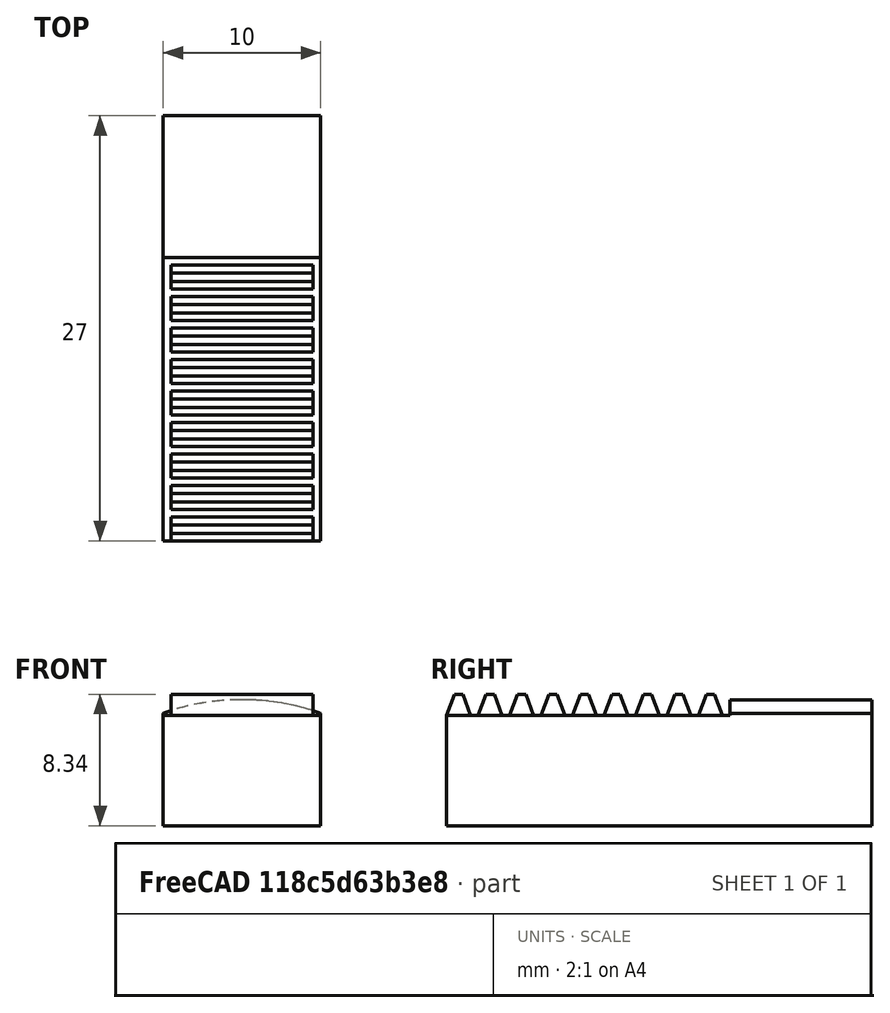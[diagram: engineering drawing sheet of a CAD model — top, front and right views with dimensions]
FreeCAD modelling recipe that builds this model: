
FCSTD DOCUMENT  (FreeCAD 0.16R4924 (Git))
Label: pin_v3p2
License: All rights reserved
LicenseURL: http://en.wikipedia.org/wiki/All_rights_reserved
objects: Part::Feature×9, Part::Box×3, Part::MultiFuse×2, Part::Cylinder×1, Part::MultiCommon×1, Part::Cut×1
note: 17 computed .brp shape members not serialized (recipe doc carries the construction recipe); baked Part::Feature solids carry a one-line shape summary decoded from their .brp

FEATURE [Part::Cylinder] Cylinder  label="rounded_top"
  Angle = 360
  Height = 40
  Placement = pos=(5,35,-7) rot=(1,0,0;1.5708rad)
  Radius = 15
FEATURE [Part::Box] Box  label="pin"
  Height = 8
  Length = 10
  Width = 27
FEATURE [Part::MultiCommon] Common  label="rounded pin"
  Shapes = -> [Cylinder,Box]
FEATURE [Part::Box] Box001  label="flat_top"
  Height = 10
  Length = 10
  Placement = pos=(0,0,7) rot=(0,0,1;0rad)
  Width = 18
FEATURE [Part::Cut] Cut
  Base = -> Common
  Placement = pos=(0,11,0) rot=(0,0,1;0rad)
  Tool = -> Box001
FEATURE [Part::Box] cube
  Height = 5
  Length = 18
  Placement = pos=(-12,-4.5,-2.5) rot=(0,0,1;0rad)
  Width = 9
FEATURE [Part::Feature] polyhedron
  Placement = pos=(-11.2451,0,2.5) rot=(0,0,1;0rad)
  shape: bbox 1.51 x 9 x 1.337 mm, 6 faces (baked)
FEATURE [Part::Feature] polyhedron001
  Placement = pos=(-9.24512,0,2.5) rot=(0,0,1;0rad)
  shape: bbox 1.51 x 9 x 1.337 mm, 6 faces (baked)
FEATURE [Part::Feature] polyhedron002
  Placement = pos=(-7.24512,0,2.5) rot=(0,0,1;0rad)
  shape: bbox 1.51 x 9 x 1.337 mm, 6 faces (baked)
FEATURE [Part::Feature] polyhedron003
  Placement = pos=(-5.24512,0,2.5) rot=(0,0,1;0rad)
  shape: bbox 1.51 x 9 x 1.337 mm, 6 faces (baked)
FEATURE [Part::Feature] polyhedron004
  Placement = pos=(-3.24512,0,2.5) rot=(0,0,1;0rad)
  shape: bbox 1.51 x 9 x 1.337 mm, 6 faces (baked)
FEATURE [Part::Feature] polyhedron005
  Placement = pos=(-1.24512,0,2.5) rot=(0,0,1;0rad)
  shape: bbox 1.51 x 9 x 1.337 mm, 6 faces (baked)
FEATURE [Part::Feature] polyhedron006
  Placement = pos=(0.754882,0,2.5) rot=(0,0,1;0rad)
  shape: bbox 1.51 x 9 x 1.337 mm, 6 faces (baked)
FEATURE [Part::Feature] polyhedron007
  Placement = pos=(2.75488,0,2.5) rot=(0,0,1;0rad)
  shape: bbox 1.51 x 9 x 1.337 mm, 6 faces (baked)
FEATURE [Part::Feature] polyhedron008
  Placement = pos=(4.75488,0,2.5) rot=(0,0,1;0rad)
  shape: bbox 1.51 x 9 x 1.337 mm, 6 faces (baked)
FEATURE [Part::MultiFuse] Fusion  label="rack"
  Placement = pos=(5,23,4.5) rot=(0,0,1;1.5708rad)
  Shapes = -> [cube,polyhedron002,polyhedron003,polyhedron004,polyhedron005,polyhedron,polyhedron007,polyhedron001,polyhedron006,polyhedron008]
FEATURE [Part::MultiFuse] Fusion001
  Shapes = -> [Fusion,Cut]
